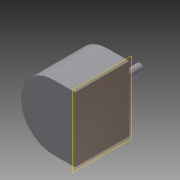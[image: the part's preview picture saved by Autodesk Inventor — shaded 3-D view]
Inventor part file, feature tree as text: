
AUTODESK INVENTOR PART (.ipt)
format: ipt  version: 2014 (Build 180170000, 170)  size: 94,208 bytes
history: native  units: mm
features: extrude x4, sketch x4, plane x2, projected_geometry x1
ambient origin geometry x8: Origin, YZ Plane, XZ Plane, XY Plane, X Axis, Y Axis, Z Axis, Center Point
bodies: Solid1 (feature_tree)
feature tree (11):
  extrude  "Extrusion1"  Depth=50.0mm TaperAngle=0.0deg
  extrude  "Extrusion2"  Depth=30.0mm TaperAngle=0.0deg
  plane  "Work Plane1"
  extrude  "Extrusion3"  [1 undecoded]
  sketch  "Sketch4"  dims[d9=10.0mm d10=0.0mm]
  plane  "Work Plane2"
  extrude  "Extrusion4"  [1 undecoded]
  sketch  "Sketch1"  dims[d0=60.0mm d1=50.0mm d2=0.0mm]
  sketch  "Sketch2"  dims[d3=7.0mm d4=30.0mm d5=0.0mm]
  sketch  "Sketch3"  dims[d6=30.0mm d7=0.0mm d8=-10.0mm]
  projected_geometry  "Projected Loop1"
note: 2 required parameter values undecoded (feature->parameter linkage not recoverable at this tier; creation-order binding heuristic only, values carry confidence <= 0.55)
